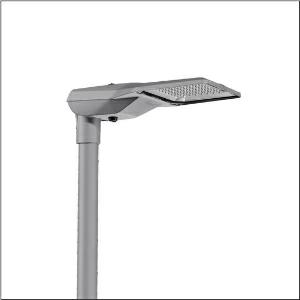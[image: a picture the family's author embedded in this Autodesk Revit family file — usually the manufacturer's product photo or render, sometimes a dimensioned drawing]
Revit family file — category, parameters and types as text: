
# Revit family: streetlight_sl_21_midi___st1_0a_5xe3d43t08mb_aa37
name_source: partatom
category: Lighting Fixtures
units: mm (PartAtom-declared; Revit-internal decimal feet)

## family parameters
Cut with Voids When Loaded = No
Host = Face
Light Source = No
Part Type = Normal
Room Calculation Point = No
Round Connector Dimension = Use Diameter
Shared = No

## types (1)
- --- (1 x LED, 20180 lm, 147 W, 4000K)
    Apparent Load = 147 VA
    CIE Flux Codes = 37 72 97 100 100
    Color Rendering = 70
    Color Temperature = 4000K
    Default Elevation = 1800 mm
    Description = Streetlight SL 21 midi, mast luminaire, primary light control with lens, of PMMA, primary optical cover: cover, of toughened safety glass, transparent, light distribution: ST1.0a, light emission: direct distribution, primary light characteristic: asymmetric, installation type: side-entry, post-top, LED, High Power LED, rated luminous flux: 20.180lm, luminous efficacy: 137lm/W, light colour: 740, colour temperature: 4000K, control: overheat protection, constant luminous flux control, time-dependent luminous flux control, flexible luminous flux parameterisation, presetting dimming logarithmic, mains connection: 230..240V, AC, 50/60Hz, start of lifetime: 147W, end of service life: 155W, reduction: 65W, luminaire housing, of diecast aluminium, powder-coated, Siteco® metallic grey (DB 702S), corrosivity category C5 mid according to DIN EN ISO 12944, please order mast flange separately, inclination adjustable: 0°, 5°, 10°, 15°, sealing non-destructively replaceable, multi-level sealing system, length: 644mm, width: 335mm, height: 110mm, mast flange for spigot size: 42mm (side-entry): 5XC10008XM4, 60/48mm (side-entry/post-top): 5XC10108XM2, 76/60mm (side-entry/post-top): 5XC10108XM1, Smart Interface below and above, protection rating (complete): IP66, insulation class (complete): insulation class II (safety insulation), certification: CE, ENEC, ENEC+, VDE, impact resistance: IK09, permissible operating ambient temperature for outdoor applications: -40..+50°C, standard-compliant lighting for roads and squares, packaging unit: 1 piece

Light Distribution: ST1.0a
    Height = 111 mm
    Lamp = 1 x LED
    Lamp Light Flux = 20180 lm
    Lamp Power = 147 W
    Lamp count = 1
    Length = 644 mm
    Luminous efficacy = 137 lm/W
    Manufacturer = Siteco
    ModVariant = No
    Model = 5XE3D43T08MB
    Number of Poles = 1
    OnlyDefault = Yes
    Power Factor = 1
    Product Name = Streetlight SL 21 midi | ST1.0a
    Product group = mast luminaire | pylon top
    ProductGroupID = 6100
    Protection Class = Protection class II
    Protection Degree = IP 66
    RLX_Detail_Level = 1
    RLX_Emergency_Light_Flux = 0 lm
    RLX_Emergency_Type = 0
    RLX_Emergency_Type_DB = No
    RlxData = <blob elided: 90965 chars, md5=bea58ba7>
    Socket = socket
    Standby Power = 0 W
    System Light Flux = 20180 lm
    System Power = 147 W
    Type Comments = factory setting: luminous flux: 100 % | dim-lin: 254 | 750 mA
    Type Image = l_1004304.jpg
    URL = http://relux.com
    VarID = @adj_141287
    Voltage = 0 V
    Weight = 0.00 kg
    Width = 336 mm

## geometry (parser evidence)
native form markers: Blend x4, Sweep x11
no freeform markers — native parametric forms only
